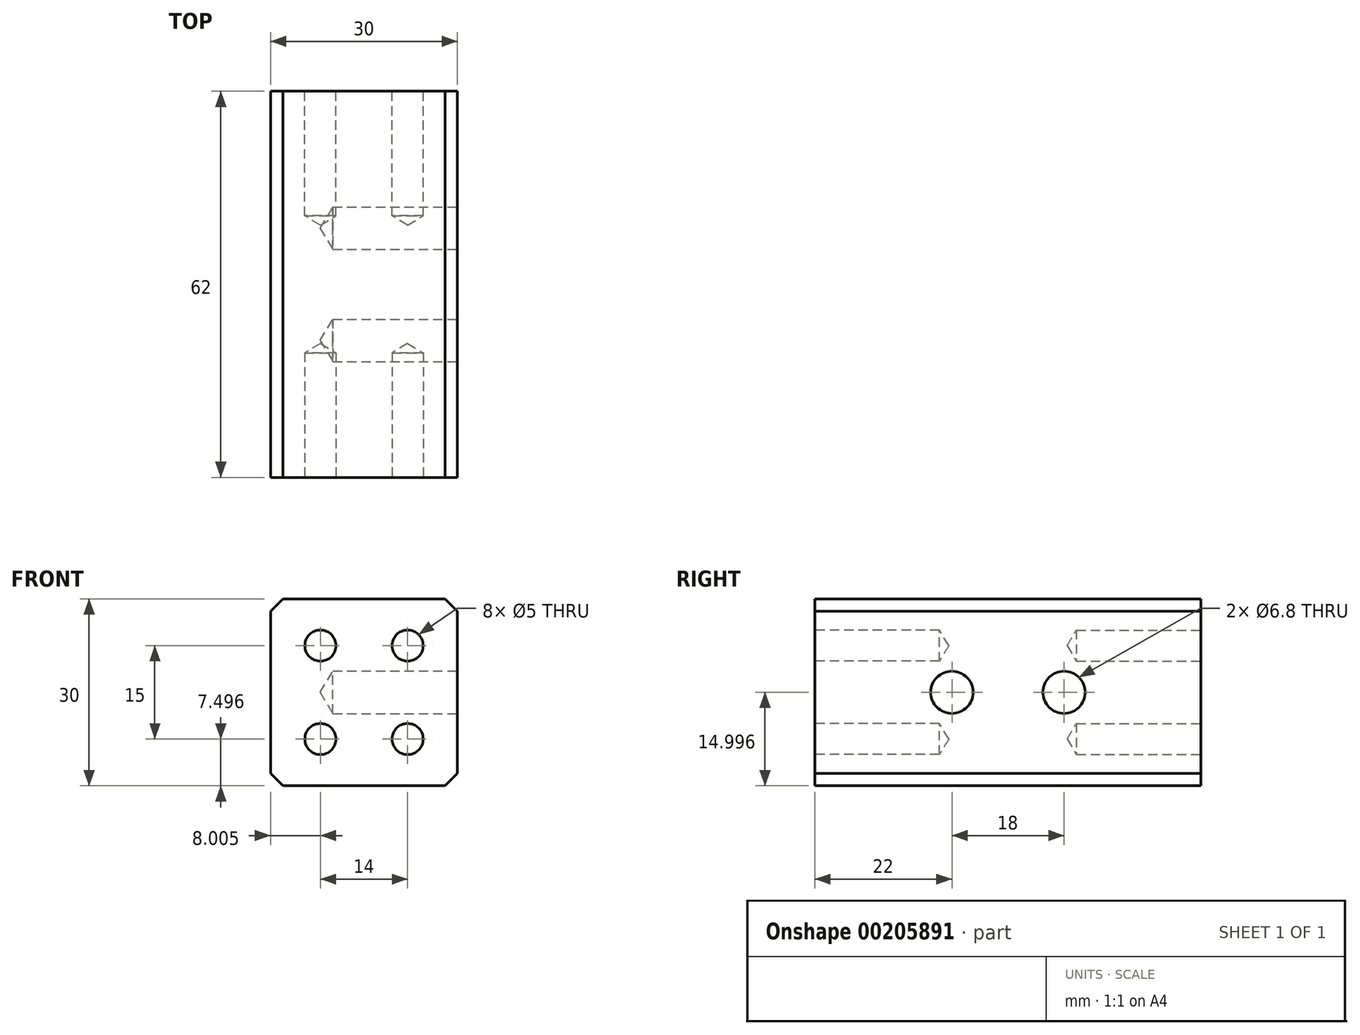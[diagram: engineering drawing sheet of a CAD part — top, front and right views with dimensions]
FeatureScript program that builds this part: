
annotation { "Feature Type Name" : "Feature", "Feature Type Description" : "" }
export const myFeature = defineFeature(function(context is Context, id is Id, definition is map)
    precondition{}
    {
        {
            var Q0;
            Q0=qCreatedBy(makeId("Front.planeOp"),FACE);
            var sketch = newSketch(context, id + "F0", { "sketchPlane" : qUnion([Q0])});
            skLineSegment(sketch, "E0.bottom", {"start": v(17.6, 18.45) * mm, "end": v(-12.4, 18.45) * mm});
            skLineSegment(sketch, "E0.top", {"start": v(17.6, -11.55) * mm, "end": v(-12.4, -11.55) * mm});
            skLineSegment(sketch, "E0.left", {"start": v(17.6, 18.45) * mm, "end": v(17.6, -11.55) * mm});
            skLineSegment(sketch, "E0.right", {"start": v(-12.4, 18.45) * mm, "end": v(-12.4, -11.55) * mm});
            skSolve(sketch);
        }
        {
            var Q0;
            Q0 = qSketchRegion(id + "F0", true);
            extrude(context, id + "F1", {"entities" : qUnion([Q0]), "depth" : 62 * mm});
        }
        {
            var Q0;
            Q0=makeQuery(id+"F1.opExtrude","CAP_FACE",FACE,{"disambiguationData":[OSD([sQuery(id+"F0.wireOp",EDGE,"E0.bottom"),sQuery(id+"F0.wireOp",EDGE,"E0.top"),sQuery(id+"F0.wireOp",EDGE,"E0.left"),sQuery(id+"F0.wireOp",EDGE,"E0.right")])],"isStart":false});
            var sketch = newSketch(context, id + "F2", { "sketchPlane" : qUnion([Q0])});
            skPoint(sketch, "E1", {"position": v(-4.4, 10.95) * mm});
            skPoint(sketch, "E2", {"position": v(9.6, 10.95) * mm});
            skPoint(sketch, "E3", {"position": v(9.6, -4.05) * mm});
            skPoint(sketch, "E4", {"position": v(-4.4, -4.05) * mm});
            skSolve(sketch);
        }
        {
            var Q0;
            Q0=sQuery(id+"F2.wireOp",VERTEX,"E1");
            var Q1;
            Q1=sQuery(id+"F2.wireOp",VERTEX,"E2");
            var Q2;
            Q2=sQuery(id+"F2.wireOp",VERTEX,"E3");
            var Q3;
            Q3=sQuery(id+"F2.wireOp",VERTEX,"E4");
            var Q4;
            Q4=makeQuery(id+"F1.opExtrude","SWEPT_BODY",BODY,{"disambiguationData":[OSD([sQuery(id+"F0.wireOp",EDGE,"E0.bottom"),sQuery(id+"F0.wireOp",EDGE,"E0.top"),sQuery(id+"F0.wireOp",EDGE,"E0.left"),sQuery(id+"F0.wireOp",EDGE,"E0.right")])]});
            hole(context, id + "F3", {"style" : HoleStyle.SIMPLE, "endStyle" : HoleEndStyle.BLIND, "standardTappedOrClearance" : lookupTablePath({ "standard" : "ISO", "engagement" : "75%", "pitch" : "1 mm", "size" : "M6", "type" : "Tapped" }), "standardBlindInLast" : lookupTablePath({ "standard" : "ISO", "engagement" : "75%", "pitch" : "1 mm", "size" : "M6", "type" : "Tapped" }), "holeDiameter" : 5 * mm, "holeDepth" : 20 * mm, "locations" : qUnion([Q0, Q1, Q2, Q3]), "scope" : qUnion([Q4]), "majorDiameter" : 6 * mm});
        }
        {
            var Q0;
            Q0=makeQuery(id+"F1.opExtrude","SWEPT_FACE",FACE,{"disambiguationData":[OSD([sQuery(id+"F0.wireOp",EDGE,"E0.left")])]});
            var sketch = newSketch(context, id + "F4", { "sketchPlane" : qUnion([Q0])});
            skPoint(sketch, "E5", {"position": v(-40, 3.45) * mm});
            skPoint(sketch, "E5.positionSnap0", {"position": v(-62, 3.45) * mm});
            skPoint(sketch, "E6", {"position": v(-22, 3.45) * mm});
            skSolve(sketch);
        }
        {
            var Q0;
            Q0=sQuery(id+"F4.wireOp",VERTEX,"E5");
            var Q1;
            Q1=sQuery(id+"F4.wireOp",VERTEX,"E6");
            var Q2;
            Q2=makeQuery(id+"F1.opExtrude","SWEPT_BODY",BODY,{"disambiguationData":[OSD([sQuery(id+"F0.wireOp",EDGE,"E0.bottom"),sQuery(id+"F0.wireOp",EDGE,"E0.top"),sQuery(id+"F0.wireOp",EDGE,"E0.left"),sQuery(id+"F0.wireOp",EDGE,"E0.right")])]});
            hole(context, id + "F5", {"style" : HoleStyle.SIMPLE, "endStyle" : HoleEndStyle.BLIND, "standardTappedOrClearance" : lookupTablePath({ "standard" : "ISO", "engagement" : "75%", "pitch" : "1.25 mm", "size" : "M8", "type" : "Tapped" }), "standardBlindInLast" : lookupTablePath({ "standard" : "ISO", "engagement" : "75%", "pitch" : "1.25 mm", "size" : "M8", "type" : "Tapped" }), "holeDiameter" : 6.8 * mm, "holeDepth" : 20 * mm, "locations" : qUnion([Q0, Q1]), "scope" : qUnion([Q2]), "majorDiameter" : 8 * mm});
        }
        {
            var Q0;
            Q0=makeQuery(id+"F1.opExtrude","CAP_FACE",FACE,{"disambiguationData":[OSD([sQuery(id+"F0.wireOp",EDGE,"E0.bottom"),sQuery(id+"F0.wireOp",EDGE,"E0.top"),sQuery(id+"F0.wireOp",EDGE,"E0.left"),sQuery(id+"F0.wireOp",EDGE,"E0.right")])],"isStart":true});
            var sketch = newSketch(context, id + "F6", { "sketchPlane" : qUnion([Q0])});
            skPoint(sketch, "E7", {"position": v(-9.6, 10.95) * mm});
            skPoint(sketch, "E8", {"position": v(4.4, 10.95) * mm});
            skPoint(sketch, "E9", {"position": v(4.4, -4.05) * mm});
            skPoint(sketch, "E10", {"position": v(-9.6, -4.05) * mm});
            skSolve(sketch);
        }
        {
            var Q0;
            Q0=sQuery(id+"F6.wireOp",VERTEX,"E7");
            var Q1;
            Q1=sQuery(id+"F6.wireOp",VERTEX,"E8");
            var Q2;
            Q2=sQuery(id+"F6.wireOp",VERTEX,"E9");
            var Q3;
            Q3=sQuery(id+"F6.wireOp",VERTEX,"E10");
            var Q4;
            Q4=makeQuery(id+"F1.opExtrude","SWEPT_BODY",BODY,{"disambiguationData":[OSD([sQuery(id+"F0.wireOp",EDGE,"E0.bottom"),sQuery(id+"F0.wireOp",EDGE,"E0.top"),sQuery(id+"F0.wireOp",EDGE,"E0.left"),sQuery(id+"F0.wireOp",EDGE,"E0.right")])]});
            hole(context, id + "F7", {"style" : HoleStyle.SIMPLE, "endStyle" : HoleEndStyle.BLIND, "standardTappedOrClearance" : lookupTablePath({ "standard" : "ISO", "engagement" : "75%", "pitch" : "1 mm", "size" : "M6", "type" : "Tapped" }), "standardBlindInLast" : lookupTablePath({ "standard" : "ISO", "engagement" : "75%", "pitch" : "1 mm", "size" : "M6", "type" : "Tapped" }), "holeDiameter" : 5 * mm, "holeDepth" : 20 * mm, "locations" : qUnion([Q0, Q1, Q2, Q3]), "scope" : qUnion([Q4]), "majorDiameter" : 6 * mm});
        }
        {
            var Q0;
            Q0=makeQuery(id+"F1.opExtrude","SWEPT_EDGE",EDGE,{"disambiguationData":[OSD([sQuery(id+"F0.wireOp",EDGE,"E0.bottom"),sQuery(id+"F0.wireOp",EDGE,"E0.right")])]});
            var Q1;
            Q1=makeQuery(id+"F1.opExtrude","SWEPT_EDGE",EDGE,{"disambiguationData":[OSD([sQuery(id+"F0.wireOp",EDGE,"E0.bottom"),sQuery(id+"F0.wireOp",EDGE,"E0.left")])]});
            var Q2;
            Q2=makeQuery(id+"F1.opExtrude","SWEPT_EDGE",EDGE,{"disambiguationData":[OSD([sQuery(id+"F0.wireOp",EDGE,"E0.top"),sQuery(id+"F0.wireOp",EDGE,"E0.left")])]});
            var Q3;
            Q3=makeQuery(id+"F1.opExtrude","SWEPT_EDGE",EDGE,{"disambiguationData":[OSD([sQuery(id+"F0.wireOp",EDGE,"E0.top"),sQuery(id+"F0.wireOp",EDGE,"E0.right")])]});
            chamfer(context, id + "F8", {"entities" : qUnion([Q0, Q1, Q2, Q3]), "width" : 2 * mm, "tangentPropagation" : true});
        }
    });
